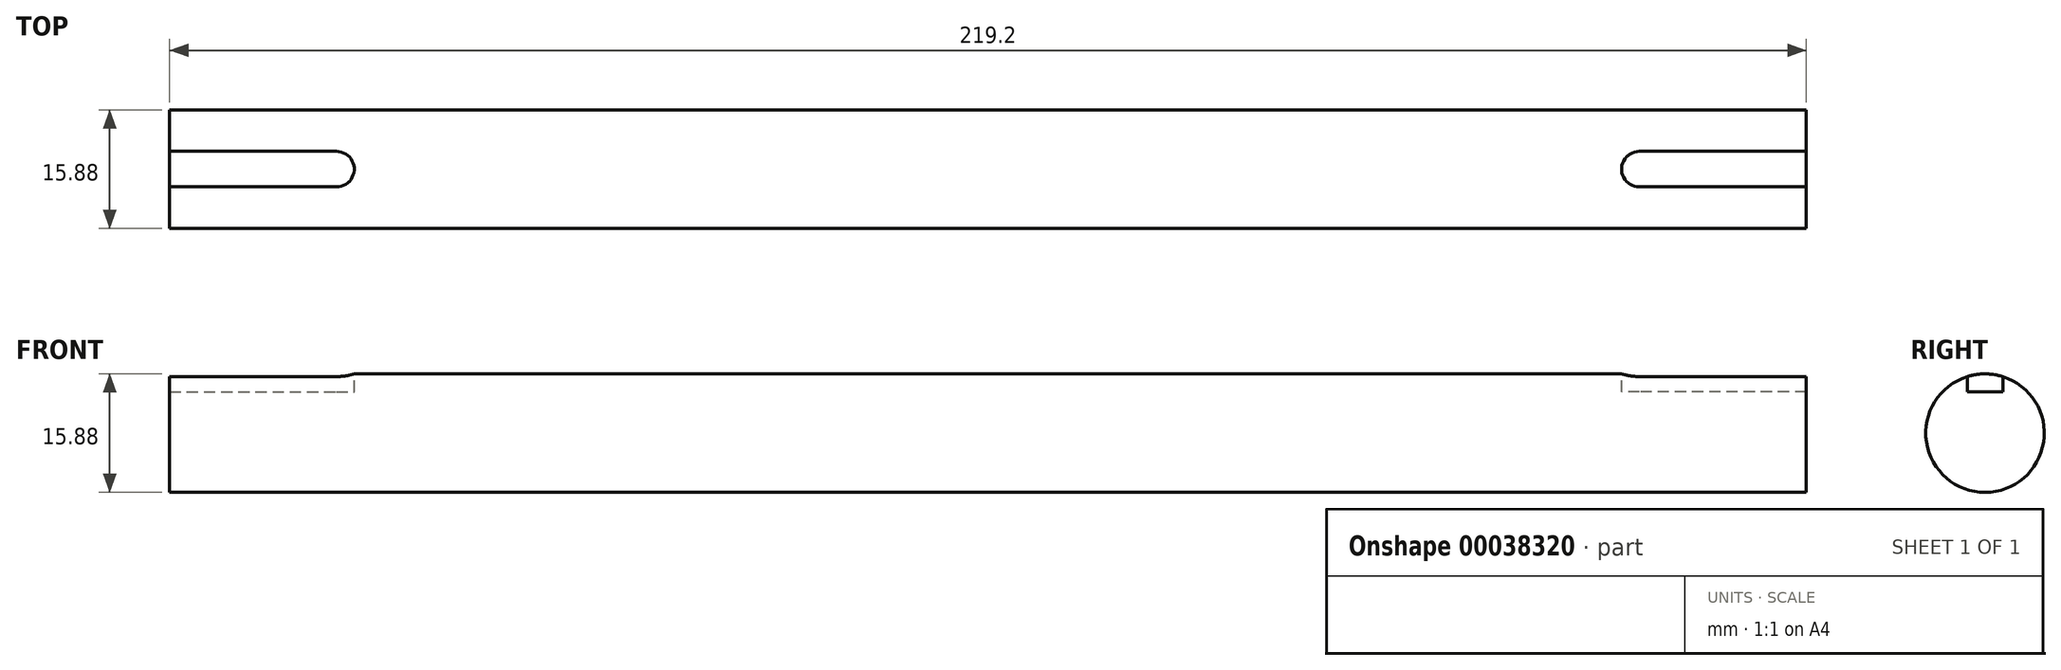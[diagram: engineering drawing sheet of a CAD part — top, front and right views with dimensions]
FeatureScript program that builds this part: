
annotation { "Feature Type Name" : "Feature", "Feature Type Description" : "" }
export const myFeature = defineFeature(function(context is Context, id is Id, definition is map)
    precondition{}
    {
        {
            var Q0;
            Q0=qCreatedBy(makeId("Right.planeOp"),FACE);
            var sketch = newSketch(context, id + "F0", { "sketchPlane" : qUnion([Q0])});
            skCircle(sketch, "E0", {"center": v(0, 0) * mm, "radius": 7.94 * mm});
            skSolve(sketch);
        }
        {
            var Q0;
            Q0 = qSketchRegion(id + "F0", true);
            extrude(context, id + "F1", {"entities" : qUnion([Q0]), "endBound" : BoundingType.SYMMETRIC, "depth" : 219.2 * mm});
        }
        {
            var Q0;
            Q0=qCreatedBy(makeId("Top.planeOp"),FACE);
            cPlane(context, id + "F2", {"entities" : qUnion([Q0]), "cplaneType" : CPlaneType.OFFSET, "offset" : 7.94 * mm, "width" : 152.4 * mm, "height" : 152.4 * mm});
        }
        {
            var Q0;
            Q0=qCreatedBy(id+"F2.planeOp",FACE);
            var sketch = newSketch(context, id + "F3", { "sketchPlane" : qUnion([Q0])});
            skLineSegment(sketch, "E1", {"start": v(119.36, 0) * mm, "end": v(-3.63, 0) * mm, "construction": true});
            skLineSegment(sketch, "E2.0", {"start": v(109.6, 7.94) * mm, "end": v(109.6, -7.94) * mm, "construction": true});
            skLineSegment(sketch, "E3", {"start": v(109.6, 0) * mm, "end": v(87.25, 0) * mm});
            skArc(sketch, "E4.0.startCap", {"start": v(109.6, 2.38) * mm, "mid": v(111.98, 0) * mm, "end": v(109.6, -2.38) * mm});
            skArc(sketch, "E4.0.endCap", {"start": v(87.25, -2.38) * mm, "mid": v(84.87, 0) * mm, "end": v(87.25, 2.38) * mm});
            skLineSegment(sketch, "E4.0.left", {"start": v(109.6, -2.38) * mm, "end": v(87.25, -2.38) * mm});
            skLineSegment(sketch, "E4.0.right", {"start": v(109.6, 2.38) * mm, "end": v(87.25, 2.38) * mm});
            skArc(sketch, "E5.MirrorCS", {"start": v(-87.25, -2.38) * mm, "mid": v(-84.87, 0) * mm, "end": v(-87.25, 2.38) * mm});
            skArc(sketch, "E6.MirrorCS", {"start": v(-109.6, 2.38) * mm, "mid": v(-111.98, 0) * mm, "end": v(-109.6, -2.38) * mm});
            skLineSegment(sketch, "E7.MirrorCS", {"start": v(-109.6, 7.94) * mm, "end": v(-109.6, -7.94) * mm});
            skLineSegment(sketch, "E8.MirrorCS", {"start": v(-109.6, 2.38) * mm, "end": v(-87.25, 2.38) * mm});
            skLineSegment(sketch, "E9.MirrorCS", {"start": v(-109.6, -2.38) * mm, "end": v(-87.25, -2.38) * mm});
            skLineSegment(sketch, "E10.MirrorCS", {"start": v(-109.6, 0) * mm, "end": v(-87.25, 0) * mm});
            skSolve(sketch);
        }
        {
            var Q0;
            Q0 = qSketchRegion(id + "F3", true);
            extrude(context, id + "F4", {"entities" : qUnion([Q0]), "operationType" : NewBodyOperationType.REMOVE, "oppositeDirection" : true, "depth" : 2.38 * mm});
        }
    });
